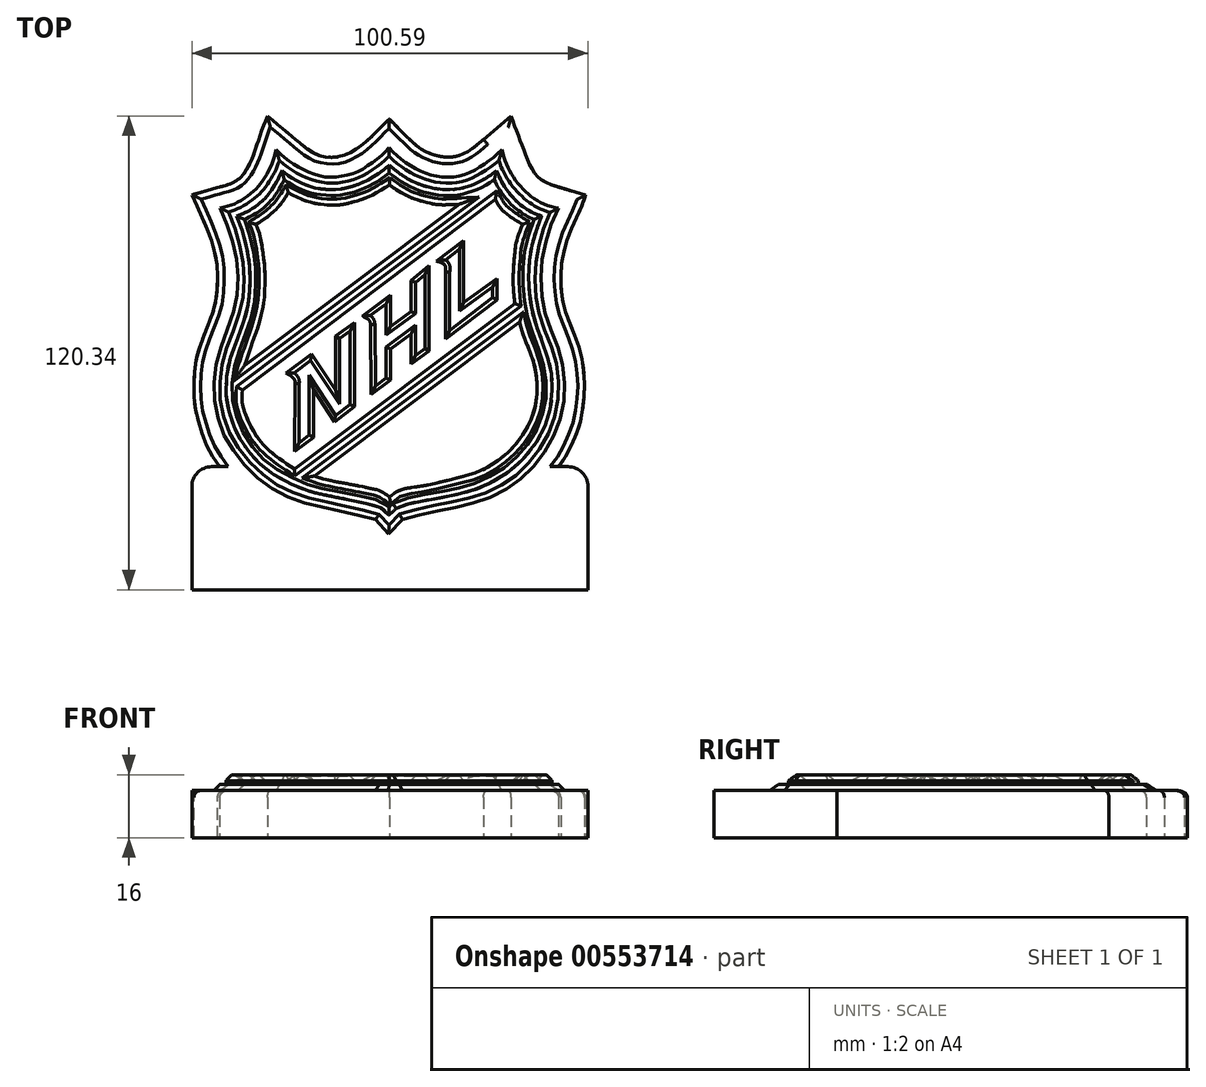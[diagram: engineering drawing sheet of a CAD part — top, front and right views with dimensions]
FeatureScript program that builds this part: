
annotation { "Feature Type Name" : "Feature", "Feature Type Description" : "" }
export const myFeature = defineFeature(function(context is Context, id is Id, definition is map)
    precondition{}
    {
        {
            var Q0;
            Q0=qCreatedBy(makeId("Top.planeOp"),FACE);
            var sketch = newSketch(context, id + "F0", { "sketchPlane" : qUnion([Q0])});
            skLineSegment(sketch, "E0", {"start": v(50, 113.85) * mm, "end": v(50, 0) * mm, "construction": true});
            skLineSegment(sketch, "E1", {"start": v(0, 56.93) * mm, "end": v(100, 56.93) * mm, "construction": true});
            skFitSpline(sketch, "E2", {"points": [v(19.23, 113.85) * mm, v(27.56, 106.9) * mm, v(30.56, 104.67) * mm, v(33.56, 103.56) * mm, v(37.49, 103.58) * mm, v(41.05, 105.05) * mm, v(45.06, 108.09) * mm, v(48.5, 111.55) * mm, v(50.17, 113.1) * mm], "startDerivative": vector(48.33, -40.51) * mm, "endDerivative": vector(17.24, 15.33) * mm});
            skFitSpline(sketch, "E3", {"points": [v(50.17, 113.1) * mm, v(52.88, 110.37) * mm, v(56.85, 106.54) * mm, v(59.8, 104.69) * mm, v(64.07, 103.49) * mm, v(69, 104.28) * mm, v(74.05, 107.95) * mm], "startDerivative": vector(16.76, -16.86) * mm, "endDerivative": vector(25.56, 22.35) * mm});
            skFitSpline(sketch, "E4", {"points": [v(74.05, 107.95) * mm, v(81.12, 113.81) * mm], "startDerivative": vector(7.07, 5.86) * mm, "endDerivative": vector(7.07, 5.86) * mm});
            skFitSpline(sketch, "E5", {"points": [v(81.12, 113.81) * mm, v(81.69, 112.23) * mm, v(82.46, 110.17) * mm, v(83.47, 107.49) * mm, v(84.8, 103.88) * mm, v(85.65, 101.74) * mm, v(87.45, 98.94) * mm, v(89.7, 97.08) * mm, v(92.96, 95.88) * mm, v(97.7, 94.47) * mm, v(100, 93.85) * mm], "startDerivative": vector(7.22, -20.27) * mm, "endDerivative": vector(22.72, -5.9) * mm});
            skFitSpline(sketch, "E6", {"points": [v(100, 93.85) * mm, v(99.63, 92.56) * mm, v(98.68, 90.12) * mm, v(97.69, 87.95) * mm, v(96.72, 85.83) * mm, v(95.29, 82.28) * mm, v(94.02, 77.13) * mm, v(93.73, 74.43) * mm, v(93.84, 69.89) * mm, v(94.57, 65.37) * mm, v(96.14, 60.78) * mm, v(97.7, 56.93) * mm, v(98.46, 54.7) * mm, v(99.33, 50.7) * mm, v(99.66, 47.48) * mm, v(99.7, 44.06) * mm, v(99.26, 39.32) * mm, v(98.41, 35.15) * mm, v(96.8, 31.22) * mm, v(94.63, 26.9) * mm, v(91.9, 23.25) * mm, v(87.6, 18.78) * mm, v(82.5, 15.03) * mm, v(77.28, 12.13) * mm, v(72.01, 10.37) * mm, v(65.55, 9) * mm, v(59.09, 7.54) * mm, v(56.38, 7.05) * mm], "startDerivative": vector(-14.58, -55.75) * mm, "endDerivative": vector(-79.32, -12.44) * mm});
            skFitSpline(sketch, "E7", {"points": [v(56.38, 7.05) * mm, v(50.17, 0.2) * mm], "startDerivative": vector(-6.21, -6.86) * mm, "endDerivative": vector(-6.21, -6.86) * mm});
            skFitSpline(sketch, "E8", {"points": [v(50.17, 0.2) * mm, v(43.77, 7.05) * mm], "startDerivative": vector(-6.4, 6.86) * mm, "endDerivative": vector(-6.4, 6.86) * mm});
            skFitSpline(sketch, "E9", {"points": [v(43.77, 7.05) * mm, v(37.64, 8.3) * mm, v(30.62, 9.78) * mm, v(24.95, 11.31) * mm, v(18.28, 14.6) * mm, v(12.57, 18.84) * mm, v(7.7, 23.96) * mm, v(4.2, 29.3) * mm, v(2.63, 33.24) * mm, v(1, 38.8) * mm, v(0.53, 43.88) * mm, v(0.99, 51.33) * mm, v(2.6, 56.93) * mm, v(4.5, 61.84) * mm, v(5.46, 64.48) * mm, v(6.23, 68.11) * mm, v(6.46, 74.89) * mm, v(5.69, 79.64) * mm, v(4.3, 84.07) * mm, v(2.05, 89.37) * mm, v(0, 93.85) * mm], "startDerivative": vector(-113.2, 22.62) * mm, "endDerivative": vector(-42.94, 93.18) * mm});
            skFitSpline(sketch, "E10", {"points": [v(0, 93.85) * mm, v(7.34, 95.93) * mm, v(11.6, 97.66) * mm, v(14.8, 102.02) * mm, v(17.5, 109.53) * mm, v(19.23, 113.85) * mm], "startDerivative": vector(34.45, 9.76) * mm, "endDerivative": vector(9.58, 22.15) * mm});
            skSolve(sketch);
        }
        {
            var Q0;
            Q0=qSketchRegion(id+"F0",true);
            extrude(context, id + "F1", {"entities" : qUnion([Q0]), "depth" : 12 * mm, "offsetDistance" : 25 * mm});
        }
        {
            var Q0;
            Q0=makeQuery(id+"F1.opExtrude","CAP_FACE",FACE,{"disambiguationData":[OSD([sQuery(id+"F0.wireOp",EDGE,"E2"),sQuery(id+"F0.wireOp",EDGE,"E3"),sQuery(id+"F0.wireOp",EDGE,"E4"),sQuery(id+"F0.wireOp",EDGE,"E5"),sQuery(id+"F0.wireOp",EDGE,"E6"),sQuery(id+"F0.wireOp",EDGE,"E7"),sQuery(id+"F0.wireOp",EDGE,"E8"),sQuery(id+"F0.wireOp",EDGE,"E9"),sQuery(id+"F0.wireOp",EDGE,"E10")])],"isStart":false});
            var sketch = newSketch(context, id + "F2", { "sketchPlane" : qUnion([Q0])});
            skFitSpline(sketch, "E11", {"points": [v(6.93, 90.68) * mm, v(9.38, 84.53) * mm, v(10.7, 79.56) * mm, v(11.45, 74.35) * mm, v(11.13, 67.25) * mm, v(10.07, 63.23) * mm, v(8.87, 59.83) * mm, v(7.68, 56.76) * mm, v(5.92, 50.72) * mm, v(5.35, 44) * mm, v(5.92, 39.1) * mm, v(7.18, 34.64) * mm, v(8.75, 31.18) * mm, v(12.14, 26.4) * mm, v(15.4, 22.83) * mm, v(20.5, 18.87) * mm, v(26.97, 15.92) * mm, v(31.8, 14.6) * mm, v(38.22, 13.15) * mm, v(44.75, 11.7) * mm, v(46.57, 11.2) * mm], "startDerivative": vector(47.57, -111.38) * mm, "endDerivative": vector(50.2, -15.05) * mm});
            skFitSpline(sketch, "E12", {"points": [v(46.57, 11.2) * mm, v(50, 7.46) * mm], "startDerivative": vector(3.43, -3.75) * mm, "endDerivative": vector(3.43, -3.75) * mm});
            skFitSpline(sketch, "E13", {"points": [v(50, 7.46) * mm, v(53.6, 11.2) * mm], "startDerivative": vector(3.6, 3.75) * mm, "endDerivative": vector(3.6, 3.75) * mm});
            skFitSpline(sketch, "E14", {"points": [v(53.6, 11.2) * mm, v(58.24, 12.46) * mm, v(64.77, 13.84) * mm, v(71.05, 15.2) * mm, v(75.23, 16.58) * mm, v(79.29, 18.56) * mm, v(83.53, 21.35) * mm, v(88.02, 26.03) * mm, v(90.66, 29.77) * mm, v(92.64, 33.67) * mm, v(93.83, 37.18) * mm, v(94.55, 40.51) * mm, v(94.93, 44.7) * mm, v(94.37, 50.79) * mm, v(93.2, 54.97) * mm, v(91.04, 60.56) * mm, v(89.53, 65.5) * mm, v(88.93, 70.58) * mm, v(88.93, 74.95) * mm, v(89.34, 78.28) * mm, v(90.56, 83.59) * mm, v(91.95, 87.54) * mm, v(93.45, 90.65) * mm], "startDerivative": vector(97.04, 28) * mm, "endDerivative": vector(40.44, 78.79) * mm});
            skFitSpline(sketch, "E15", {"points": [v(6.93, 90.68) * mm, v(10.55, 91.69) * mm, v(15.37, 94.79) * mm, v(18.32, 98.34) * mm, v(20.3, 102.26) * mm, v(21.3, 105.7) * mm], "startDerivative": vector(18.82, 3.64) * mm, "endDerivative": vector(4.63, 18.8) * mm});
            skFitSpline(sketch, "E16", {"points": [v(21.3, 105.7) * mm, v(22.88, 104.22) * mm, v(25.74, 101.97) * mm, v(30.3, 99.55) * mm, v(33.76, 98.64) * mm, v(36.89, 98.6) * mm, v(41.37, 99.68) * mm, v(44.15, 101.14) * mm, v(47.55, 103.59) * mm, v(50.13, 106.23) * mm], "startDerivative": vector(17.16, -16.8) * mm, "endDerivative": vector(21.31, 24.02) * mm});
            skFitSpline(sketch, "E17", {"points": [v(50.13, 106.23) * mm, v(51.12, 105.06) * mm, v(52.88, 103.37) * mm, v(55.35, 101.62) * mm, v(57.8, 100.26) * mm, v(61, 99.05) * mm, v(64.11, 98.55) * mm, v(67.14, 98.69) * mm, v(70.55, 99.75) * mm, v(73.46, 101.34) * mm, v(75.97, 103.12) * mm, v(78.88, 105.7) * mm], "startDerivative": vector(14.11, -17.2) * mm, "endDerivative": vector(28.39, 26.46) * mm});
            skFitSpline(sketch, "E18", {"points": [v(78.88, 105.7) * mm, v(79.72, 102.72) * mm, v(81.03, 99.75) * mm, v(83.76, 95.97) * mm, v(87.65, 92.68) * mm, v(91.85, 90.9) * mm, v(93.45, 90.65) * mm], "startDerivative": vector(5, -19.54) * mm, "endDerivative": vector(12.63, -1.1) * mm});
            skSolve(sketch);
        }
        {
            var Q0;
            Q0=qSketchRegion(id+"F2",true);
            extrude(context, id + "F3", {"entities" : qUnion([Q0]), "operationType" : NewBodyOperationType.ADD, "depth" : 1.5 * mm, "offsetDistance" : 25 * mm});
        }
        {
            var Q0;
            Q0=makeQuery(id+"F3.opExtrude","CAP_FACE",FACE,{"disambiguationData":[OSD([sQuery(id+"F2.wireOp",EDGE,"E11"),sQuery(id+"F2.wireOp",EDGE,"E12"),sQuery(id+"F2.wireOp",EDGE,"E13"),sQuery(id+"F2.wireOp",EDGE,"E14"),sQuery(id+"F2.wireOp",EDGE,"E15"),sQuery(id+"F2.wireOp",EDGE,"E16"),sQuery(id+"F2.wireOp",EDGE,"E17"),sQuery(id+"F2.wireOp",EDGE,"E18")])],"isStart":false});
            chamfer(context, id + "F4", {"entities" : qUnion([Q0]), "width" : 1.7 * mm, "tangentPropagation" : true});
        }
        {
            var Q0;
            Q0=makeQuery(id+"F1.opExtrude","CAP_EDGE",EDGE,{"disambiguationData":[OSD([sQuery(id+"F0.wireOp",EDGE,"E6")])],"isStart":false});
            var Q1;
            Q1=makeQuery(id+"F1.opExtrude","CAP_EDGE",EDGE,{"disambiguationData":[OSD([sQuery(id+"F0.wireOp",EDGE,"E7")])],"isStart":false});
            var Q2;
            Q2=makeQuery(id+"F1.opExtrude","CAP_EDGE",EDGE,{"disambiguationData":[OSD([sQuery(id+"F0.wireOp",EDGE,"E9")])],"isStart":false});
            var Q3;
            Q3=makeQuery(id+"F1.opExtrude","CAP_EDGE",EDGE,{"disambiguationData":[OSD([sQuery(id+"F0.wireOp",EDGE,"E10")])],"isStart":false});
            var Q4;
            Q4=makeQuery(id+"F1.opExtrude","CAP_EDGE",EDGE,{"disambiguationData":[OSD([sQuery(id+"F0.wireOp",EDGE,"E2")])],"isStart":false});
            var Q5;
            Q5=makeQuery(id+"F1.opExtrude","CAP_EDGE",EDGE,{"disambiguationData":[OSD([sQuery(id+"F0.wireOp",EDGE,"E3")])],"isStart":false});
            var Q6;
            Q6=makeQuery(id+"F1.opExtrude","CAP_EDGE",EDGE,{"disambiguationData":[OSD([sQuery(id+"F0.wireOp",EDGE,"E5")])],"isStart":false});
            var Q7;
            Q7=makeQuery(id+"F1.opExtrude","CAP_EDGE",EDGE,{"disambiguationData":[OSD([sQuery(id+"F0.wireOp",EDGE,"E8")])],"isStart":false});
            var Q8;
            Q8=makeQuery(id+"F1.opExtrude","CAP_EDGE",EDGE,{"disambiguationData":[OSD([sQuery(id+"F0.wireOp",EDGE,"E4")])],"isStart":false});
            fillet(context, id + "F5", {"entities" : qUnion([Q0, Q1, Q2, Q3, Q4, Q5, Q6, Q7, Q8]), "radius" : 1.7 * mm, "tangentPropagation" : true, "allowEdgeOverflow" : false});
        }
        {
            var Q0;
            Q0=makeQuery(id+"F3.opExtrude","CAP_FACE",FACE,{"disambiguationData":[OSD([sQuery(id+"F2.wireOp",EDGE,"E11"),sQuery(id+"F2.wireOp",EDGE,"E12"),sQuery(id+"F2.wireOp",EDGE,"E13"),sQuery(id+"F2.wireOp",EDGE,"E14"),sQuery(id+"F2.wireOp",EDGE,"E15"),sQuery(id+"F2.wireOp",EDGE,"E16"),sQuery(id+"F2.wireOp",EDGE,"E17"),sQuery(id+"F2.wireOp",EDGE,"E18")])],"isStart":false});
            var sketch = newSketch(context, id + "F6", { "sketchPlane" : qUnion([Q0])});
            skFitSpline(sketch, "E19", {"points": [v(11.37, 88.45) * mm, v(12.75, 84.84) * mm, v(14.07, 79.6) * mm, v(14.73, 73.93) * mm, v(14.36, 66.8) * mm, v(13.25, 61.9) * mm, v(11.3, 56.49) * mm, v(9.2, 50.2) * mm, v(8.65, 44.05) * mm, v(9.31, 39.27) * mm, v(10.66, 35.04) * mm, v(12, 32.1) * mm, v(14.54, 28.46) * mm, v(17.27, 25.53) * mm, v(21.73, 22.25) * mm, v(28.36, 19.06) * mm, v(33.06, 17.76) * mm, v(39.61, 16.42) * mm, v(45.66, 15.12) * mm, v(48.33, 14.14) * mm, v(50, 12.48) * mm], "startDerivative": vector(32.13, -77.93) * mm, "endDerivative": vector(45.27, -54.13) * mm});
            skFitSpline(sketch, "E20", {"points": [v(50, 12.48) * mm, v(50.86, 13.19) * mm, v(51.9, 14.14) * mm], "startDerivative": vector(1.78, 1.45) * mm, "endDerivative": vector(2, 1.88) * mm});
            skFitSpline(sketch, "E21", {"points": [v(51.9, 14.14) * mm, v(54.14, 15.04) * mm, v(57.27, 15.8) * mm, v(61.04, 16.52) * mm, v(66.07, 17.5) * mm, v(70.78, 18.64) * mm, v(74.2, 19.92) * mm, v(79.17, 22.64) * mm, v(84, 26.6) * mm, v(88.33, 32.31) * mm, v(90.05, 36.22) * mm, v(91.3, 41) * mm, v(91.48, 46.26) * mm, v(91.02, 50.12) * mm, v(89.72, 54.5) * mm, v(88.39, 58.21) * mm, v(86.99, 62.32) * mm, v(86.04, 66.7) * mm, v(85.64, 70.54) * mm, v(85.59, 74.12) * mm, v(85.93, 78.58) * mm, v(86.63, 82) * mm, v(88, 86.25) * mm, v(88.86, 88.5) * mm], "startDerivative": vector(65.22, 29.34) * mm, "endDerivative": vector(25.15, 61.86) * mm});
            skFitSpline(sketch, "E22", {"points": [v(88.86, 88.5) * mm, v(86.66, 89.3) * mm, v(83.49, 91.33) * mm, v(81.45, 93.3) * mm, v(79.35, 96.03) * mm, v(78.07, 98.49) * mm, v(77.41, 100.02) * mm], "startDerivative": vector(-13.59, 4.04) * mm, "endDerivative": vector(-4.71, 11.2) * mm});
            skFitSpline(sketch, "E23", {"points": [v(77.41, 100.02) * mm, v(75.76, 98.79) * mm, v(72.88, 97.1) * mm, v(69.79, 95.86) * mm, v(66.4, 95.22) * mm, v(63.71, 95.22) * mm, v(60.17, 95.8) * mm, v(56.66, 97) * mm, v(53.74, 98.6) * mm, v(51.2, 100.52) * mm, v(50.15, 101.42) * mm], "startDerivative": vector(-18.12, -14.24) * mm, "endDerivative": vector(-13.41, 11.88) * mm});
            skFitSpline(sketch, "E24", {"points": [v(50.15, 101.42) * mm, v(49.1, 100.53) * mm, v(46.36, 98.57) * mm, v(42.82, 96.77) * mm, v(39.83, 95.75) * mm, v(36.52, 95.21) * mm, v(33.3, 95.32) * mm, v(31.09, 95.67) * mm, v(28.7, 96.5) * mm, v(26.17, 97.7) * mm, v(24.13, 99.03) * mm, v(22.89, 100.02) * mm], "startDerivative": vector(-14.26, -12.25) * mm, "endDerivative": vector(-16.53, 13.74) * mm});
            skFitSpline(sketch, "E25", {"points": [v(22.89, 100.02) * mm, v(22.15, 98.38) * mm, v(20.5, 95.49) * mm, v(19.15, 93.63) * mm, v(16.66, 91.26) * mm, v(13.63, 89.4) * mm, v(11.37, 88.45) * mm], "startDerivative": vector(-4.62, -11.1) * mm, "endDerivative": vector(-13.9, -5.32) * mm});
            skFitSpline(sketch, "E26", {"points": [v(24.48, 94.37) * mm, v(22.17, 91.05) * mm, v(18.5, 87.76) * mm, v(16.26, 86.34) * mm], "startDerivative": vector(-5.87, -9.67) * mm, "endDerivative": vector(-7.52, -4.35) * mm});
            skFitSpline(sketch, "E27", {"points": [v(16.26, 86.34) * mm, v(17.23, 83.65) * mm, v(18.13, 78.35) * mm, v(18.5, 75.02) * mm, v(18.5, 69.45) * mm, v(17.98, 65) * mm, v(16.64, 59.93) * mm, v(14.77, 54.66) * mm, v(13.39, 50.51) * mm], "startDerivative": vector(10.37, -23.68) * mm, "endDerivative": vector(-10.58, -32.85) * mm});
            skLineSegment(sketch, "E28", {"start": v(13.39, 50.51) * mm, "end": v(68.05, 91.51) * mm});
            skFitSpline(sketch, "E29", {"points": [v(24.48, 94.37) * mm, v(28.95, 92.31) * mm, v(33.44, 91.38) * mm, v(37.62, 91.33) * mm, v(42.5, 92.49) * mm, v(45.93, 93.82) * mm, v(50.23, 96.4) * mm], "startDerivative": vector(25.4, -13.36) * mm, "endDerivative": vector(25.52, 16.34) * mm});
            skFitSpline(sketch, "E30", {"points": [v(50.23, 96.4) * mm, v(52.32, 94.93) * mm, v(55.92, 93.07) * mm, v(60.14, 91.78) * mm, v(63.07, 91.33) * mm, v(68.05, 91.51) * mm], "startDerivative": vector(11.74, -8.7) * mm, "endDerivative": vector(23.3, 1.55) * mm});
            skLineSegment(sketch, "E31", {"start": v(12.82, 44.3) * mm, "end": v(77.05, 92.7) * mm});
            skFitSpline(sketch, "E32", {"points": [v(77.05, 92.7) * mm, v(78.84, 90.02) * mm, v(83.95, 86.35) * mm], "startDerivative": vector(3.36, -6.48) * mm, "endDerivative": vector(10.08, -6.24) * mm});
            skFitSpline(sketch, "E33", {"points": [v(83.95, 86.35) * mm, v(82.43, 81.87) * mm, v(82.09, 79.59) * mm, v(81.6, 72.89) * mm, v(82.02, 66.26) * mm], "startDerivative": vector(-7.5, -20.4) * mm, "endDerivative": vector(2.3, -21.83) * mm});
            skLineSegment(sketch, "E34", {"start": v(82.02, 66.26) * mm, "end": v(26.08, 24.2) * mm});
            skFitSpline(sketch, "E35", {"points": [v(12.82, 44.3) * mm, v(12.82, 40.7) * mm, v(15.24, 34.56) * mm, v(18.97, 29.52) * mm, v(26.08, 24.2) * mm], "startDerivative": vector(-1.94, -17.52) * mm, "endDerivative": vector(26.12, -17.5) * mm});
            skLineSegment(sketch, "E36", {"start": v(31.11, 22.4) * mm, "end": v(83.25, 61.56) * mm});
            skFitSpline(sketch, "E37", {"points": [v(83.25, 61.56) * mm, v(84.22, 58.1) * mm, v(86.22, 53.14) * mm, v(87.26, 49.34) * mm, v(87.67, 44.85) * mm, v(86.64, 38.08) * mm, v(82.56, 30.83) * mm, v(79.04, 27.38) * mm, v(73.52, 23.79) * mm, v(67.02, 21.85) * mm, v(60.8, 20.33) * mm, v(56.39, 19.57) * mm, v(52.45, 18.67) * mm, v(50.24, 17.09) * mm], "startDerivative": vector(11.94, -50.95) * mm, "endDerivative": vector(-35.18, -31.83) * mm});
            skFitSpline(sketch, "E38", {"points": [v(50.24, 17.09) * mm, v(49.45, 17.64) * mm, v(48.07, 18.54) * mm, v(45.86, 19.16) * mm, v(40.26, 20.3) * mm, v(33.94, 21.54) * mm, v(31.11, 22.4) * mm], "startDerivative": vector(-7.9, 5.34) * mm, "endDerivative": vector(-15.3, 5.29) * mm});
            skSolve(sketch);
        }
        {
            var Q0;
            Q0=qSketchRegion(id+"F6",true);
            extrude(context, id + "F7", {"entities" : qUnion([Q0]), "operationType" : NewBodyOperationType.ADD, "depth" : 2.5 * mm, "offsetDistance" : 25 * mm});
        }
        {
            var Q0;
            Q0=qCreatedBy(makeId("Top.planeOp"),FACE);
            var sketch = newSketch(context, id + "F8", { "sketchPlane" : qUnion([Q0])});
            skLineSegment(sketch, "E39", {"start": v(26.13, 28.62) * mm, "end": v(30.9, 32.23) * mm});
            skLineSegment(sketch, "E40", {"start": v(30.9, 32.23) * mm, "end": v(30.9, 44.39) * mm});
            skLineSegment(sketch, "E41", {"start": v(30.9, 44.39) * mm, "end": v(36.22, 36.19) * mm});
            skLineSegment(sketch, "E42", {"start": v(36.22, 36.19) * mm, "end": v(41.26, 40.02) * mm});
            skLineSegment(sketch, "E43", {"start": v(41.26, 40.02) * mm, "end": v(41.26, 61.46) * mm});
            skLineSegment(sketch, "E44", {"start": v(41.26, 61.46) * mm, "end": v(36.44, 57.95) * mm});
            skLineSegment(sketch, "E45", {"start": v(36.44, 57.95) * mm, "end": v(36.44, 44.3) * mm});
            skLineSegment(sketch, "E46", {"start": v(36.44, 44.3) * mm, "end": v(30.36, 53.4) * mm});
            skLineSegment(sketch, "E47", {"start": v(30.36, 53.4) * mm, "end": v(23.97, 48.53) * mm});
            skFitSpline(sketch, "E48", {"points": [v(23.97, 48.53) * mm, v(24.91, 48) * mm, v(26.04, 46.96) * mm, v(26.17, 45.96) * mm], "startDerivative": vector(2.8, -1.47) * mm, "endDerivative": vector(-0.17, -3.3) * mm});
            skLineSegment(sketch, "E49", {"start": v(26.13, 28.62) * mm, "end": v(26.17, 45.96) * mm});
            skLineSegment(sketch, "E50", {"start": v(45.51, 43.13) * mm, "end": v(50.42, 46.78) * mm});
            skLineSegment(sketch, "E51", {"start": v(50.42, 46.78) * mm, "end": v(50.42, 54.62) * mm});
            skLineSegment(sketch, "E52", {"start": v(50.42, 54.62) * mm, "end": v(55.65, 58.54) * mm});
            skLineSegment(sketch, "E53", {"start": v(55.65, 58.54) * mm, "end": v(55.65, 50.84) * mm});
            skLineSegment(sketch, "E54", {"start": v(55.65, 50.84) * mm, "end": v(60.29, 54.21) * mm});
            skLineSegment(sketch, "E55", {"start": v(60.29, 54.21) * mm, "end": v(60.29, 75.84) * mm});
            skLineSegment(sketch, "E56", {"start": v(60.29, 75.84) * mm, "end": v(55.65, 72.14) * mm});
            skLineSegment(sketch, "E57", {"start": v(55.65, 72.14) * mm, "end": v(55.65, 64.26) * mm});
            skLineSegment(sketch, "E58", {"start": v(55.65, 64.26) * mm, "end": v(50.42, 60.39) * mm});
            skLineSegment(sketch, "E59", {"start": v(50.42, 60.39) * mm, "end": v(50.42, 68.36) * mm});
            skLineSegment(sketch, "E60", {"start": v(50.42, 68.36) * mm, "end": v(43.33, 63.1) * mm});
            skFitSpline(sketch, "E61", {"points": [v(43.33, 63.1) * mm, v(44.12, 62.6) * mm, v(45.02, 62) * mm, v(45.42, 60.84) * mm], "startDerivative": vector(2.4, -1.7) * mm, "endDerivative": vector(0.69, -3.69) * mm});
            skLineSegment(sketch, "E62", {"start": v(45.42, 60.84) * mm, "end": v(45.51, 43.13) * mm});
            skLineSegment(sketch, "E63", {"start": v(77.46, 72.58) * mm, "end": v(77.46, 67.17) * mm});
            skLineSegment(sketch, "E64", {"start": v(77.46, 67.17) * mm, "end": v(64.39, 57.2) * mm});
            skLineSegment(sketch, "E65", {"start": v(64.39, 57.2) * mm, "end": v(64.39, 74.3) * mm});
            skLineSegment(sketch, "E66", {"start": v(62.2, 76.98) * mm, "end": v(69.05, 82.28) * mm});
            skLineSegment(sketch, "E67", {"start": v(69.05, 82.28) * mm, "end": v(69.05, 66.48) * mm});
            skLineSegment(sketch, "E68", {"start": v(69.05, 66.48) * mm, "end": v(77.46, 72.58) * mm});
            skFitSpline(sketch, "E69", {"points": [v(62.2, 76.98) * mm, v(63.58, 76.55) * mm, v(64.39, 75.7) * mm, v(64.39, 74.3) * mm], "startDerivative": vector(4.23, -0.9) * mm, "endDerivative": vector(-0.62, -4.37) * mm});
            skSolve(sketch);
        }
        {
            var Q0;
            Q0=qSketchRegion(id+"F8",true);
            extrude(context, id + "F9", {"entities" : qUnion([Q0]), "operationType" : NewBodyOperationType.ADD, "depth" : 15.7 * mm, "offsetDistance" : 25 * mm});
        }
        {
            var Q0;
            Q0=makeQuery(id+"F9.opExtrude","CAP_FACE",FACE,{"disambiguationData":[OSD([sQuery(id+"F8.wireOp",EDGE,"E39"),sQuery(id+"F8.wireOp",EDGE,"E40"),sQuery(id+"F8.wireOp",EDGE,"E41"),sQuery(id+"F8.wireOp",EDGE,"E42"),sQuery(id+"F8.wireOp",EDGE,"E43"),sQuery(id+"F8.wireOp",EDGE,"E44"),sQuery(id+"F8.wireOp",EDGE,"E45"),sQuery(id+"F8.wireOp",EDGE,"E46"),sQuery(id+"F8.wireOp",EDGE,"E47"),sQuery(id+"F8.wireOp",EDGE,"E48"),sQuery(id+"F8.wireOp",EDGE,"E49")])],"isStart":false});
            var Q1;
            Q1=makeQuery(id+"F9.opExtrude","CAP_FACE",FACE,{"disambiguationData":[OSD([sQuery(id+"F8.wireOp",EDGE,"E50"),sQuery(id+"F8.wireOp",EDGE,"E51"),sQuery(id+"F8.wireOp",EDGE,"E52"),sQuery(id+"F8.wireOp",EDGE,"E53"),sQuery(id+"F8.wireOp",EDGE,"E54"),sQuery(id+"F8.wireOp",EDGE,"E55"),sQuery(id+"F8.wireOp",EDGE,"E56"),sQuery(id+"F8.wireOp",EDGE,"E57"),sQuery(id+"F8.wireOp",EDGE,"E58"),sQuery(id+"F8.wireOp",EDGE,"E59"),sQuery(id+"F8.wireOp",EDGE,"E60"),sQuery(id+"F8.wireOp",EDGE,"E61"),sQuery(id+"F8.wireOp",EDGE,"E62")])],"isStart":false});
            var Q2;
            Q2=makeQuery(id+"F9.opExtrude","CAP_FACE",FACE,{"disambiguationData":[OSD([sQuery(id+"F8.wireOp",EDGE,"E63"),sQuery(id+"F8.wireOp",EDGE,"E64"),sQuery(id+"F8.wireOp",EDGE,"E65"),sQuery(id+"F8.wireOp",EDGE,"E66"),sQuery(id+"F8.wireOp",EDGE,"E67"),sQuery(id+"F8.wireOp",EDGE,"E68"),sQuery(id+"F8.wireOp",EDGE,"E69")])],"isStart":false});
            chamfer(context, id + "F10", {"entities" : qUnion([Q0, Q1, Q2]), "width" : 1.1 * mm, "tangentPropagation" : true});
        }
        {
            var Q0;
            Q0=makeQuery(id+"F7.opExtrude","CAP_FACE",FACE,{"disambiguationData":[OSD([sQuery(id+"F6.wireOp",EDGE,"E19"),sQuery(id+"F6.wireOp",EDGE,"E20"),sQuery(id+"F6.wireOp",EDGE,"E21"),sQuery(id+"F6.wireOp",EDGE,"E22"),sQuery(id+"F6.wireOp",EDGE,"E23"),sQuery(id+"F6.wireOp",EDGE,"E24"),sQuery(id+"F6.wireOp",EDGE,"E25"),sQuery(id+"F6.wireOp",EDGE,"E26"),sQuery(id+"F6.wireOp",EDGE,"E27"),sQuery(id+"F6.wireOp",EDGE,"E28"),sQuery(id+"F6.wireOp",EDGE,"E29"),sQuery(id+"F6.wireOp",EDGE,"E30"),sQuery(id+"F6.wireOp",EDGE,"E31"),sQuery(id+"F6.wireOp",EDGE,"E32"),sQuery(id+"F6.wireOp",EDGE,"E33"),sQuery(id+"F6.wireOp",EDGE,"E34"),sQuery(id+"F6.wireOp",EDGE,"E35"),sQuery(id+"F6.wireOp",EDGE,"E36"),sQuery(id+"F6.wireOp",EDGE,"E37"),sQuery(id+"F6.wireOp",EDGE,"E38")])],"isStart":false});
            chamfer(context, id + "F11", {"entities" : qUnion([Q0]), "width" : 1.5 * mm, "tangentPropagation" : true});
        }
        {
            var Q0;
            Q0=qCreatedBy(makeId("Top.planeOp"),FACE);
            var sketch = newSketch(context, id + "F12", { "sketchPlane" : qUnion([Q0])});
            skLineSegment(sketch, "E70", {"start": v(50.3, 0) * mm, "end": v(50.3, -16.78) * mm});
            skLineSegment(sketch, "E71", {"start": v(50.3, -6.5) * mm, "end": v(0, -6.5) * mm});
            skLineSegment(sketch, "E72", {"start": v(0, -6.5) * mm, "end": v(0, 24.78) * mm});
            skLineSegment(sketch, "E73", {"start": v(0, 24.78) * mm, "end": v(50.9, 24.78) * mm});
            skLineSegment(sketch, "E74.MirrorCS", {"start": v(50.3, -6.5) * mm, "end": v(100.6, -6.5) * mm});
            skLineSegment(sketch, "E75.MirrorCS", {"start": v(100.6, -6.5) * mm, "end": v(100.6, 24.78) * mm});
            skLineSegment(sketch, "E76.MirrorCS", {"start": v(100.6, 24.78) * mm, "end": v(49.7, 24.78) * mm});
            skSolve(sketch);
        }
        {
            var Q0;
            Q0=qSketchRegion(id+"F12",true);
            extrude(context, id + "F13", {"entities" : qUnion([Q0]), "operationType" : NewBodyOperationType.ADD, "depth" : 12 * mm, "offsetDistance" : 25 * mm});
        }
        {
            var Q0;
            Q0=makeQuery(id+"F13.opExtrude","SWEPT_EDGE",EDGE,{"disambiguationData":[OSD([sQuery(id+"F12.wireOp",EDGE,"E72"),sQuery(id+"F12.wireOp",EDGE,"E73")])]});
            var Q1;
            Q1=makeQuery(id+"F13.opExtrude","SWEPT_EDGE",EDGE,{"disambiguationData":[OSD([sQuery(id+"F12.wireOp",EDGE,"E75.MirrorCS"),sQuery(id+"F12.wireOp",EDGE,"E76.MirrorCS")])]});
            fillet(context, id + "F14", {"entities" : qUnion([Q0, Q1]), "radius" : 5 * mm, "tangentPropagation" : true, "allowEdgeOverflow" : false});
        }
    });
